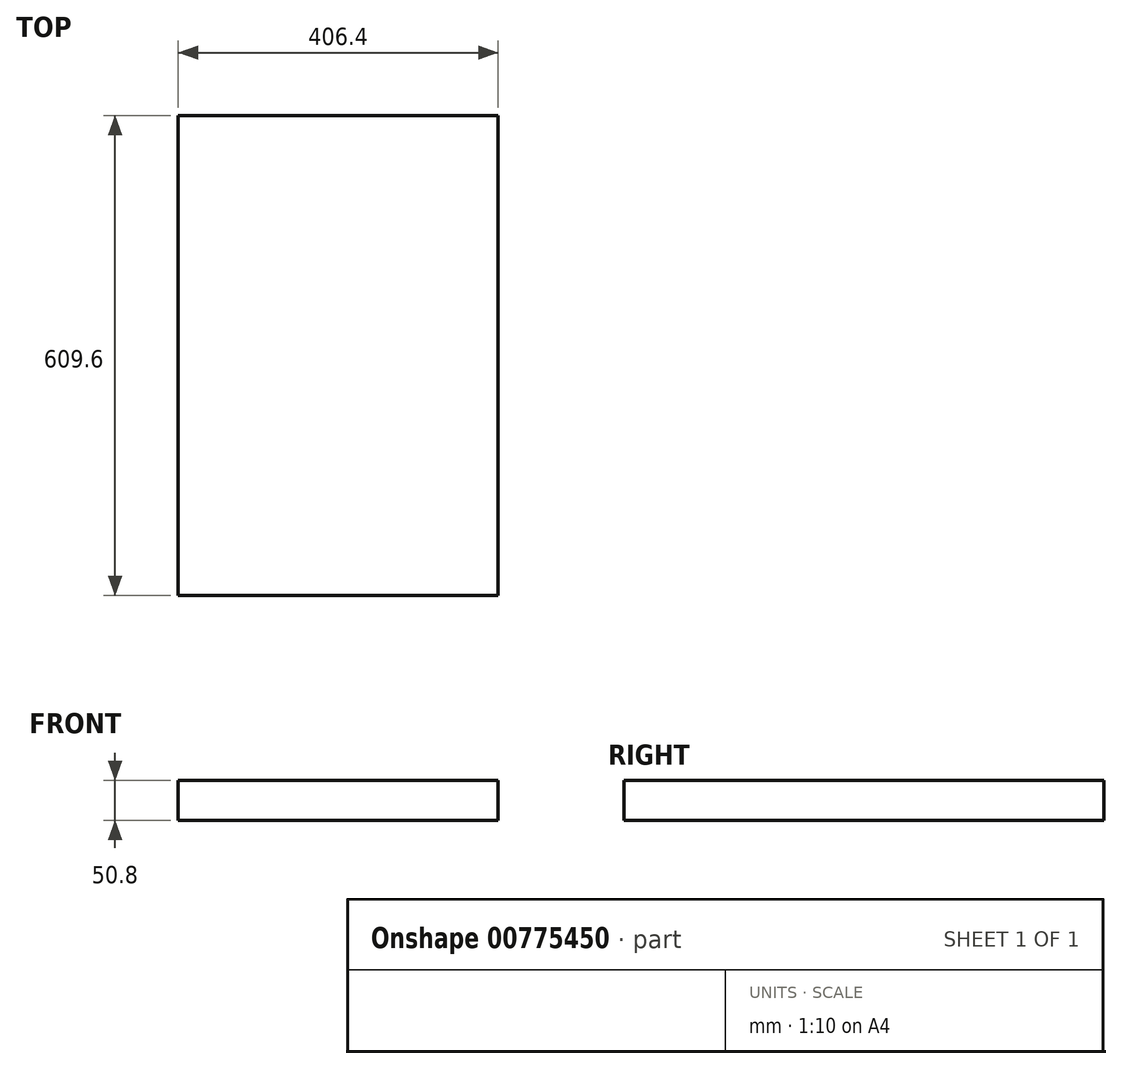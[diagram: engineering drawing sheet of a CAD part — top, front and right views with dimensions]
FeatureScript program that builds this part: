
annotation { "Feature Type Name" : "Feature", "Feature Type Description" : "" }
export const myFeature = defineFeature(function(context is Context, id is Id, definition is map)
    precondition{}
    {
        {
            var Q0;
            Q0=qCreatedBy(makeId("Front.planeOp"),FACE);
            var sketch = newSketch(context, id + "F0", { "sketchPlane" : qUnion([Q0])});
            skLineSegment(sketch, "E0.bottom", {"start": v(-203.2, 25.4) * mm, "end": v(203.2, 25.4) * mm});
            skLineSegment(sketch, "E0.top", {"start": v(-203.2, -25.4) * mm, "end": v(203.2, -25.4) * mm});
            skLineSegment(sketch, "E0.left", {"start": v(-203.2, 25.4) * mm, "end": v(-203.2, -25.4) * mm});
            skLineSegment(sketch, "E0.right", {"start": v(203.2, 25.4) * mm, "end": v(203.2, -25.4) * mm});
            skPoint(sketch, "E0.middle", {"position": v(0, 0) * mm});
            skSolve(sketch);
        }
        {
            var Q0;
            Q0=makeQuery(id+"F0.imprint","IMPRINT",FACE,{"disambiguationData":[TD([[makeQuery(id+"F0.imprint","IMPRINT",EDGE,{"derivedFrom":sQuery(id+"F0.wireOp",EDGE,"E0.bottom")}),-1.0]])]});
            extrude(context, id + "F1", {"entities" : qUnion([Q0]), "flatOperationType" : FlatOperationType.REMOVE, "depth" : 609.6 * mm, "offsetDistance" : 25.4 * mm, "domain" : OperationDomain.MODEL});
        }
    });
